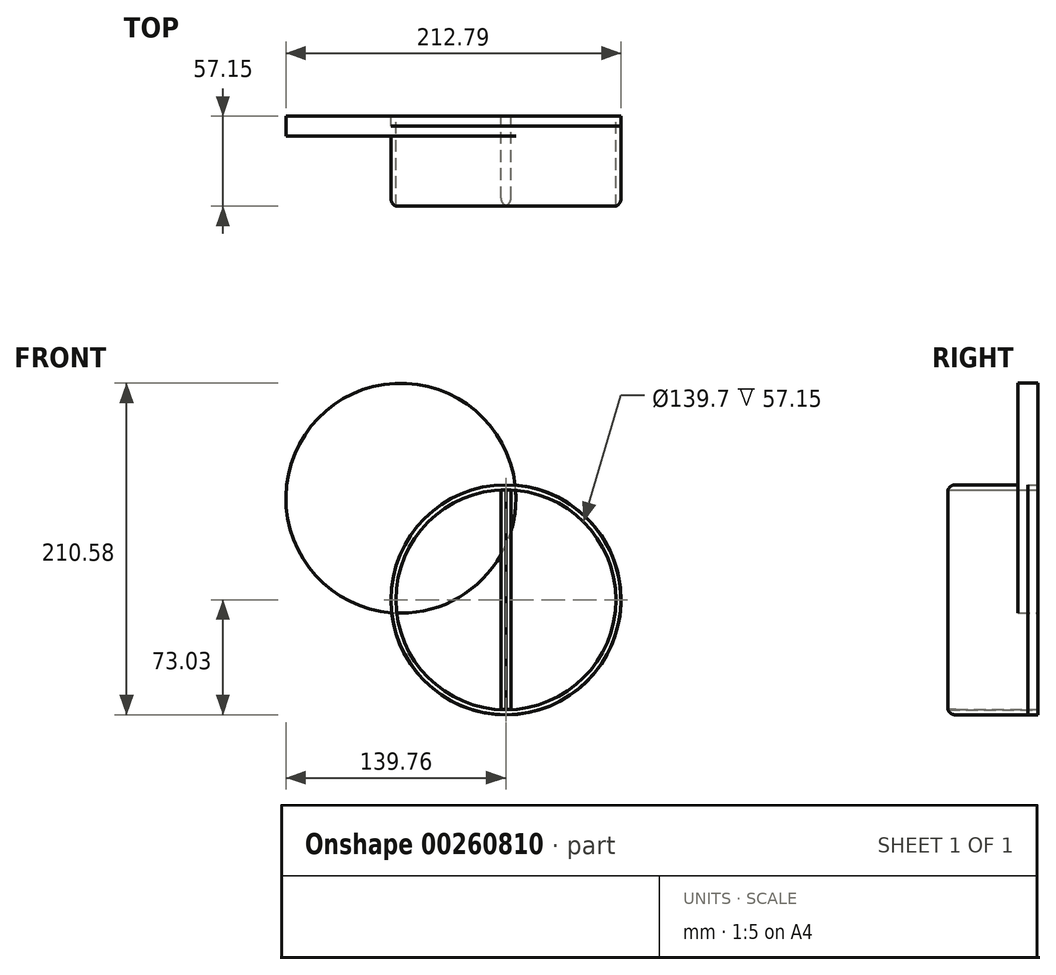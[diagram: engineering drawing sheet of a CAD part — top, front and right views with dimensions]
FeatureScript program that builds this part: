
annotation { "Feature Type Name" : "Feature", "Feature Type Description" : "" }
export const myFeature = defineFeature(function(context is Context, id is Id, definition is map)
    precondition{}
    {
        {
            var Q0;
            Q0=qCreatedBy(makeId("Front.planeOp"),FACE);
            var sketch = newSketch(context, id + "F0", { "sketchPlane" : qUnion([Q0])});
            skCircle(sketch, "E0", {"center": v(0, 0) * mm, "radius": 73.03 * mm});
            skCircle(sketch, "E1", {"center": v(0, 0) * mm, "radius": 69.85 * mm});
            skLineSegment(sketch, "E2.bottom", {"start": v(3.18, -69.78) * mm, "end": v(-3.17, -69.78) * mm});
            skLineSegment(sketch, "E2.top", {"start": v(3.17, 69.78) * mm, "end": v(-3.18, 69.78) * mm});
            skLineSegment(sketch, "E2.left", {"start": v(3.18, -69.78) * mm, "end": v(3.17, 69.78) * mm});
            skLineSegment(sketch, "E2.right", {"start": v(-3.17, -69.78) * mm, "end": v(-3.18, 69.78) * mm});
            skSolve(sketch);
        }
        {
            var Q0;
            Q0=makeQuery(id+"F0.imprint","IMPRINT",FACE,{"disambiguationData":[TD([[makeQuery(id+"F0.imprint","IMPRINT",EDGE,{"derivedFrom":sQuery(id+"F0.wireOp",EDGE,"E0")}),1.0]])]});
            var Q1;
            Q1=makeQuery(id+"F0.imprint","IMPRINT",FACE,{"disambiguationData":[TD([[makeQuery(id+"F0.imprint","IMPRINT",EDGE,{"derivedFrom":sQuery(id+"F0.wireOp",EDGE,"E2.bottom")}),-1.0]])]});
            extrude(context, id + "F1", {"entities" : qUnion([Q0, Q1]), "depth" : 57.15 * mm});
        }
        {
            var Q0;
            Q0=qCreatedBy(makeId("Front.planeOp"),FACE);
            var sketch = newSketch(context, id + "F2", { "sketchPlane" : qUnion([Q0])});
            skCircle(sketch, "E3", {"center": v(0, 0) * mm, "radius": 73.03 * mm});
            skSolve(sketch);
        }
        {
            var Q0;
            Q0=makeQuery(id+"F2.imprint","IMPRINT",FACE,{"disambiguationData":[TD([[makeQuery(id+"F2.imprint","IMPRINT",EDGE,{"derivedFrom":sQuery(id+"F2.wireOp",EDGE,"E3")}),1.0]])]});
            extrude(context, id + "F3", {"entities" : qUnion([Q0]), "depth" : 6.35 * mm});
        }
        {
            var Q0;
            Q0=makeQuery(id+"F1.opExtrude","CAP_EDGE",EDGE,{"disambiguationData":[OSD([sQuery(id+"F0.wireOp",EDGE,"E2.right")])],"isStart":false});
            var Q1;
            Q1=makeQuery(id+"F1.opExtrude","CAP_EDGE",EDGE,{"disambiguationData":[OSD([sQuery(id+"F0.wireOp",EDGE,"E2.left")])],"isStart":false});
            var Q2;
            Q2=makeQuery(id+"F1.opExtrude","CAP_EDGE",EDGE,{"disambiguationData":[OSD([sQuery(id+"F0.wireOp",EDGE,"E0")])],"isStart":false});
            fillet(context, id + "F4", {"entities" : qUnion([Q0, Q1, Q2]), "radius" : 5.08 * mm, "tangentPropagation" : true, "allowEdgeOverflow" : false});
        }
        {
            var Q0;
            Q0=qCreatedBy(makeId("Front.planeOp"),FACE);
            var sketch = newSketch(context, id + "F5", { "sketchPlane" : qUnion([Q0])});
            skCircle(sketch, "E4", {"center": v(-66.74, 64.52) * mm, "radius": 73.03 * mm});
            skSolve(sketch);
        }
        {
            var Q0;
            Q0=makeQuery(id+"F5.imprint","IMPRINT",FACE,{"disambiguationData":[TD([[makeQuery(id+"F5.imprint","IMPRINT",EDGE,{"derivedFrom":sQuery(id+"F5.wireOp",EDGE,"E4")}),1.0]])]});
            extrude(context, id + "F6", {"entities" : qUnion([Q0]), "depth" : 12.7 * mm});
        }
    });
